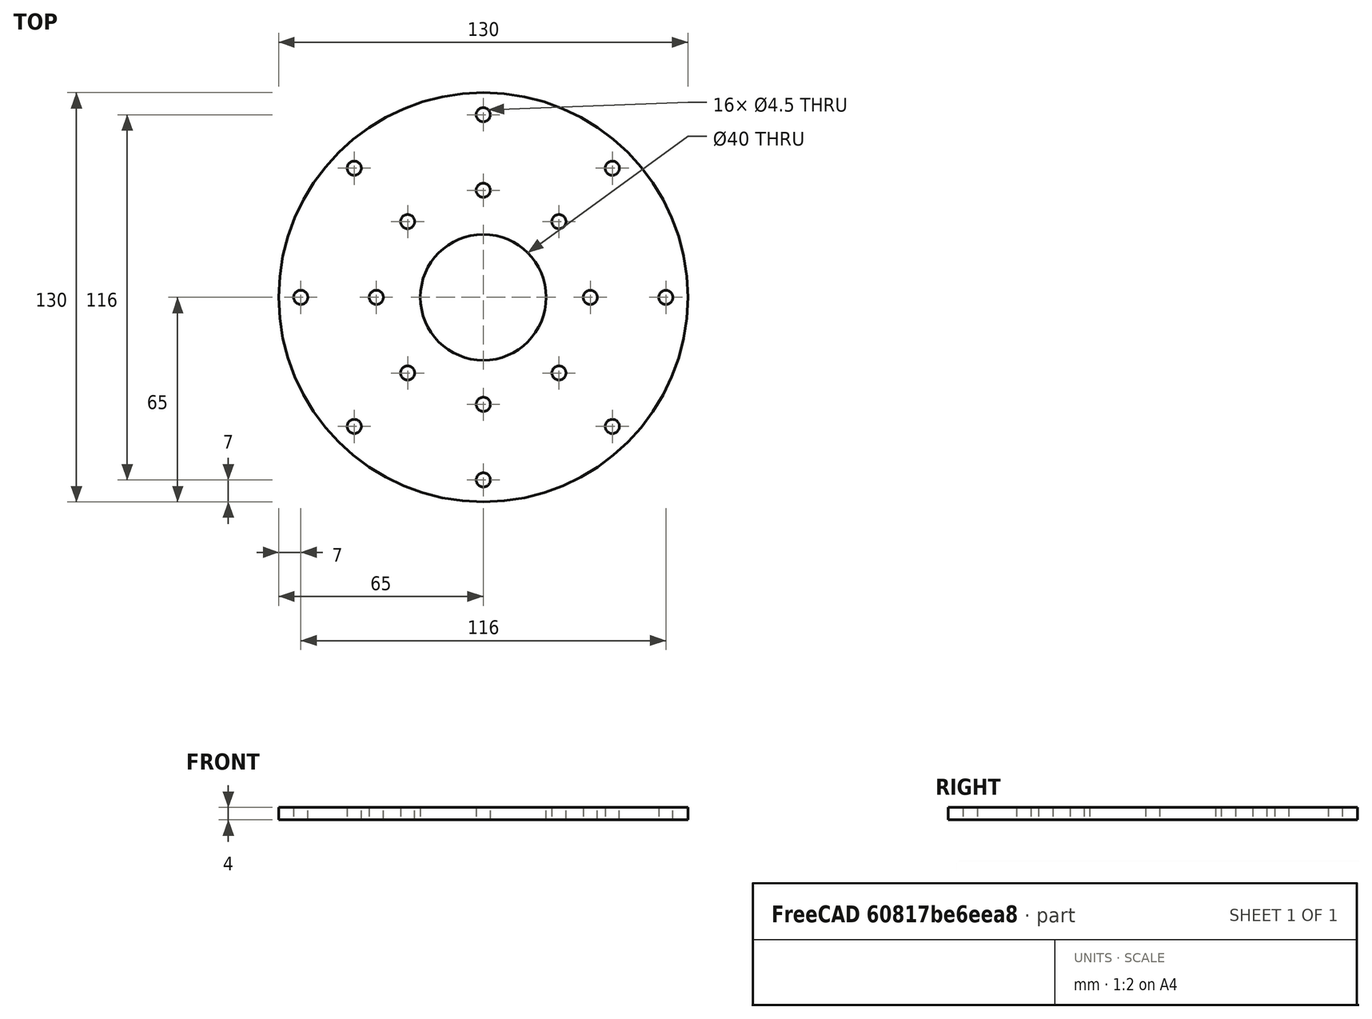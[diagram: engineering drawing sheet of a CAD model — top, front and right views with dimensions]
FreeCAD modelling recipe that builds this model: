
FCSTD DOCUMENT  (FreeCAD 0.18.4R)
Label: top_plate_LightDome
License: CreativeCommons Attribution-ShareAlike
LicenseURL: http://creativecommons.org/licenses/by-sa/4.0/
objects: TechDraw::DrawViewDimension×6, Sketcher::SketchObject×1, Part::Extrusion×1, TechDraw::DrawSVGTemplate×1, TechDraw::DrawViewPart×1, TechDraw::DrawViewAnnotation×1, TechDraw::DrawPage×1
note: 2 computed .brp shape members not serialized (recipe doc carries the construction recipe); baked Part::Feature solids carry a one-line shape summary decoded from their .brp

FEATURE [Sketcher::SketchObject] Sketch
  sketch-geometry (27):
    g0: Circle CenterX=0 CenterY=0 CenterZ=0 NormalX=0 NormalY=0 NormalZ=1 AngleXU=0 Radius=20
    g1: LineSegment [constr] StartX=-70 StartY=70 StartZ=0 EndX=70 EndY=70 EndZ=0
    g2: LineSegment [constr] StartX=70 StartY=70 StartZ=0 EndX=70 EndY=-70 EndZ=0
    g3: LineSegment [constr] StartX=70 StartY=-70 StartZ=0 EndX=-70 EndY=-70 EndZ=0
    g4: LineSegment [constr] StartX=-70 StartY=-70 StartZ=0 EndX=-70 EndY=70 EndZ=0
    g5: LineSegment [constr] StartX=-70 StartY=70 StartZ=0 EndX=70 EndY=-70 EndZ=0
    g6: LineSegment [constr] StartX=70 StartY=70 StartZ=0 EndX=-70 EndY=-70 EndZ=0
    g7: GeomPoint X=0 Y=0 Z=0
    g8: Circle [constr] CenterX=0 CenterY=0 CenterZ=0 NormalX=0 NormalY=0 NormalZ=1 AngleXU=0 Radius=34
    g9: Circle CenterX=0 CenterY=0 CenterZ=0 NormalX=0 NormalY=0 NormalZ=1 AngleXU=0 Radius=65
    g10: Circle CenterX=-24.0416 CenterY=24.0416 CenterZ=0 NormalX=0 NormalY=0 NormalZ=1 AngleXU=0 Radius=2.25
    g11: Circle CenterX=0 CenterY=34 CenterZ=0 NormalX=0 NormalY=0 NormalZ=1 AngleXU=0 Radius=2.25
    g12: Circle CenterX=34 CenterY=0 CenterZ=0 NormalX=0 NormalY=0 NormalZ=1 AngleXU=0 Radius=2.25
    g13: Circle CenterX=0 CenterY=-34 CenterZ=0 NormalX=0 NormalY=0 NormalZ=1 AngleXU=0 Radius=2.25
    g14: Circle CenterX=-24.0416 CenterY=-24.0416 CenterZ=0 NormalX=0 NormalY=0 NormalZ=1 AngleXU=0 Radius=2.25
    g15: Circle CenterX=-34 CenterY=0 CenterZ=0 NormalX=0 NormalY=0 NormalZ=1 AngleXU=0 Radius=2.25
    g16: Circle CenterX=24.0416 CenterY=-24.0416 CenterZ=0 NormalX=0 NormalY=0 NormalZ=1 AngleXU=0 Radius=2.25
    g17: Circle CenterX=24.0416 CenterY=24.0416 CenterZ=0 NormalX=0 NormalY=0 NormalZ=1 AngleXU=0 Radius=2.25
    g18: Circle [constr] CenterX=0 CenterY=0 CenterZ=0 NormalX=0 NormalY=0 NormalZ=1 AngleXU=0 Radius=58
    g19: Circle CenterX=41.0122 CenterY=41.0122 CenterZ=0 NormalX=0 NormalY=0 NormalZ=1 AngleXU=0 Radius=2.25
    g20: Circle CenterX=-58 CenterY=0 CenterZ=0 NormalX=0 NormalY=0 NormalZ=1 AngleXU=0 Radius=2.25
    g21: Circle CenterX=0 CenterY=-58 CenterZ=0 NormalX=0 NormalY=0 NormalZ=1 AngleXU=0 Radius=2.25
    g22: Circle CenterX=-41.0122 CenterY=-41.0122 CenterZ=0 NormalX=0 NormalY=0 NormalZ=1 AngleXU=0 Radius=2.25
    g23: Circle CenterX=-41.0122 CenterY=41.0122 CenterZ=0 NormalX=0 NormalY=0 NormalZ=1 AngleXU=0 Radius=2.25
    g24: Circle CenterX=41.0122 CenterY=-41.0122 CenterZ=0 NormalX=0 NormalY=0 NormalZ=1 AngleXU=0 Radius=2.25
    g25: Circle CenterX=0 CenterY=58 CenterZ=0 NormalX=0 NormalY=0 NormalZ=1 AngleXU=0 Radius=2.25
    g26: Circle CenterX=58 CenterY=0 CenterZ=0 NormalX=0 NormalY=0 NormalZ=1 AngleXU=0 Radius=2.25
  constraints (75):
    c: Coincident(g0,g-1)
    c: Radius(g0) = 20
    c: Coincident(g1,g2)
    c: Coincident(g2,g3)
    c: Coincident(g3,g4)
    c: Coincident(g4,g1)
    c: Horizontal(g1)
    c: Horizontal(g3)
    c: Vertical(g2)
    c: Vertical(g4)
    c: PointOnObject(g7,g5)
    c: PointOnObject(g7,g6)
    c: Coincident(g6,g1)
    c: Coincident(g5,g1)
    c: Coincident(g6,g3)
    c: Coincident(g5,g2)
    c: Coincident(g7,g0)
    c: Equal(g1,g4)
    c: Equal(g4,g2)
    c: Equal(g2,g3)
    c: DistanceX(g1,g1) = 140
    c: Radius(g8) = 34
    c: Coincident(g8,g0)
    c: Radius(g9) = 65
    c: Coincident(g9,g0)
    c: Radius(g10) = 2.25
    c: PointOnObject(g10,g8)
    c: PointOnObject(g10,g5)
    c: Radius(g11) = 2.25
    c: PointOnObject(g11,g-2)
    c: PointOnObject(g11,g8)
    c: Radius(g17) = 2.25
    c: PointOnObject(g17,g6)
    c: PointOnObject(g17,g8)
    c: Radius(g12) = 2.25
    c: PointOnObject(g12,g-1)
    c: PointOnObject(g12,g8)
    c: Radius(g16) = 2.25
    c: PointOnObject(g16,g5)
    c: PointOnObject(g16,g8)
    c: Radius(g13) = 2.25
    c: PointOnObject(g13,g-2)
    c: PointOnObject(g13,g8)
    c: Radius(g14) = 2.25
    c: PointOnObject(g14,g6)
    c: PointOnObject(g14,g8)
    c: Radius(g15) = 2.25
    c: PointOnObject(g15,g-1)
    c: PointOnObject(g15,g8)
    c: Radius(g18) = 58
    c: Coincident(g18,g0)
    c: Radius(g19) = 2.25
    c: PointOnObject(g19,g18)
    c: PointOnObject(g19,g6)
    c: Radius(g26) = 2.25
    c: PointOnObject(g26,g18)
    c: PointOnObject(g26,g-1)
    c: Radius(g24) = 2.25
    c: PointOnObject(g24,g18)
    c: PointOnObject(g24,g5)
    c: Radius(g25) = 2.25
    c: PointOnObject(g25,g18)
    c: PointOnObject(g25,g-2)
    c: Radius(g23) = 2.25
    c: PointOnObject(g23,g5)
    c: PointOnObject(g23,g18)
    c: Radius(g20) = 2.25
    c: PointOnObject(g20,g18)
    c: PointOnObject(g20,g-1)
    c: Radius(g22) = 2.25
    c: PointOnObject(g22,g18)
    c: PointOnObject(g22,g6)
    c: Radius(g21) = 2.25
    c: PointOnObject(g21,g18)
    c: PointOnObject(g21,g-2)
FEATURE [Part::Extrusion] Extrude
  Base = -> Sketch
  Dir = (0,0,1)
  DirMode = 2
  FaceMakerClass = Part::FaceMakerBullseye
  LengthFwd = 4
  LengthRev = 0
  Solid = true
  Symmetric = false
FEATURE [TechDraw::DrawSVGTemplate] Template
  EditableTexts = AUTHOR_NAME=Norman Rembarz; DN=1; DRAWING_TITLE=Project Regreen SensoLAB; FC-DATE=28/10/2020; FC-REV=REV A; FC-SC=1:1; FC-SH=1; FC-SI=A4; FreeCAD_DRAWING=for light-dome module; PN=LAB-LD-TP; SI-1=acrylic top-plate; SI-3=REGREEN PROJECT of EU
  Height = 210
  Orientation = 1
  Width = 297
FEATURE [TechDraw::DrawViewPart] View
  CoarseView = false
  Direction = (0,0,1)
  Focus = 100
  HardHidden = false
  IsoCount = 0
  IsoHidden = false
  IsoVisible = false
  LockPosition = false
  Perspective = false
  Rotation = 0
  ScaleType = 0
  SeamHidden = false
  SeamVisible = false
  SmoothHidden = false
  SmoothVisible = false
  Source = -> [Sketch]
  X = 82.3298
  Y = 118.404
FEATURE [TechDraw::DrawViewDimension] Dimension
  Arbitrary = false
  FormatSpec = ⌀%.2f
  LockPosition = false
  MeasureType = 1
  OverTolerance = 0
  References2D = -> [View]
  Rotation = 0
  ScaleType = 0
  Type = 5
  UnderTolerance = 0
  X = 93.8298
  Y = 65.1064
FEATURE [TechDraw::DrawViewDimension] Dimension001
  Arbitrary = false
  FormatSpec = ⌀%.2f
  LockPosition = false
  MeasureType = 1
  OverTolerance = 0
  References2D = -> [View]
  Rotation = 0
  ScaleType = 0
  Type = 5
  UnderTolerance = 0
  X = 94.6809
  Y = 55.3191
FEATURE [TechDraw::DrawViewDimension] Dimension002
  Arbitrary = false
  FormatSpec = ⌀%.2f
  LockPosition = false
  MeasureType = 1
  OverTolerance = 0
  References2D = -> [View]
  Rotation = 0
  ScaleType = 0
  Type = 5
  UnderTolerance = 0
  X = 94.2553
  Y = 27.8723
FEATURE [TechDraw::DrawViewDimension] Dimension003
  Arbitrary = false
  FormatSpec = ⌀%.2f
  LockPosition = false
  MeasureType = 1
  OverTolerance = 0
  References2D = -> [View]
  Rotation = 0
  ScaleType = 0
  Type = 5
  UnderTolerance = 0
  X = 94.4681
  Y = 21.0638
FEATURE [TechDraw::DrawViewDimension] Dimension004
  Arbitrary = false
  FormatSpec = %.2f
  LockPosition = false
  MeasureType = 1
  OverTolerance = 0
  References2D = -> [View]
  Rotation = 0
  ScaleType = 0
  Type = 2
  UnderTolerance = 0
  X = 94.4681
  Y = -10.4043
FEATURE [TechDraw::DrawViewDimension] Dimension005
  Arbitrary = false
  FormatSpec = %.2f
  LockPosition = false
  MeasureType = 1
  OverTolerance = 0
  References2D = -> [View]
  Rotation = 0
  ScaleType = 0
  Type = 2
  UnderTolerance = 0
  X = 106.596
  Y = -33.2553
FEATURE [TechDraw::DrawViewAnnotation] Annotation
  Font = osifont
  LineSpace = 80
  LockPosition = false
  MaxWidth = -1
  Rotation = 0
  ScaleType = 0
  Text = thickness of acrylic | material 4mm
  TextSize = 5
  TextStyle = 0
  X = 246.16
  Y = 69.2553
FEATURE [TechDraw::DrawPage] Page
  KeepUpdated = true
  ProjectionType = 0
  Template = -> Template
  Views = -> [View,Dimension,Dimension001,Dimension002,Dimension003,Dimension004,Dimension005,Annotation]
